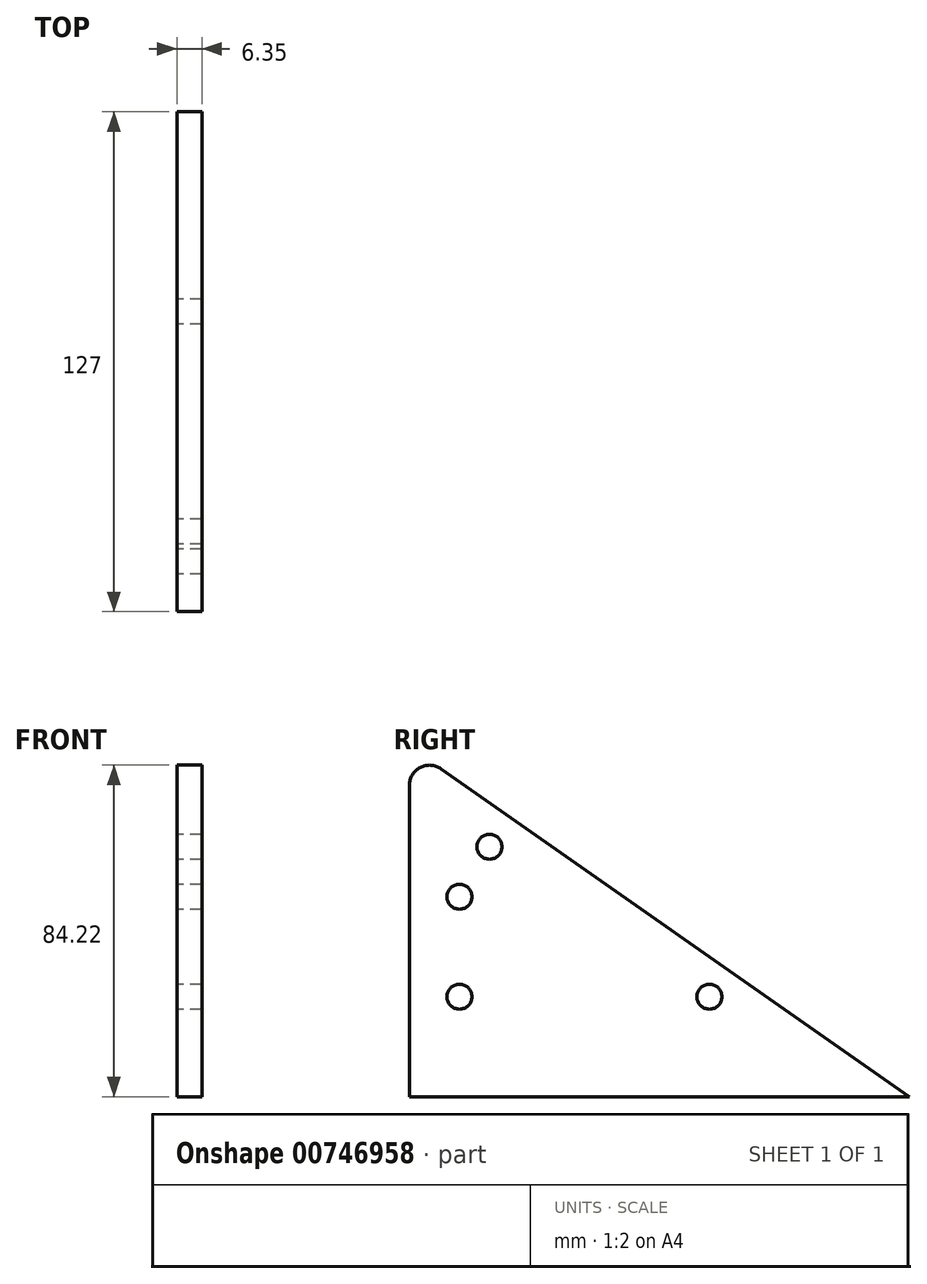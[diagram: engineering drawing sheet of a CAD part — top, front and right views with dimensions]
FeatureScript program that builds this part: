
annotation { "Feature Type Name" : "Feature", "Feature Type Description" : "" }
export const myFeature = defineFeature(function(context is Context, id is Id, definition is map)
    precondition{}
    {
        {
            var Q0;
            Q0=qCreatedBy(makeId("Right.planeOp"),FACE);
            var sketch = newSketch(context, id + "F0", { "sketchPlane" : qUnion([Q0])});
            skLineSegment(sketch, "E0.bottom", {"start": v(63.5, -44.45) * mm, "end": v(-63.5, -44.45) * mm});
            skLineSegment(sketch, "E0.right", {"start": v(-63.5, -44.45) * mm, "end": v(-63.5, 44.45) * mm});
            skPoint(sketch, "E0.middle", {"position": v(0, 0) * mm});
            skLineSegment(sketch, "E1", {"start": v(-63.5, 44.45) * mm, "end": v(63.5, -44.45) * mm});
            skCircle(sketch, "E2", {"center": v(-50.8, -19.05) * mm, "radius": 3.18 * mm});
            skCircle(sketch, "E3", {"center": v(-43.18, 19.05) * mm, "radius": 3.18 * mm});
            skCircle(sketch, "E4", {"center": v(-50.8, 6.35) * mm, "radius": 3.18 * mm});
            skCircle(sketch, "E5", {"center": v(12.7, -19.05) * mm, "radius": 3.18 * mm});
            skPoint(sketch, "E0.left.end.orphan", {"position": v(63.5, 44.45) * mm});
            skSolve(sketch);
        }
        {
            var Q0;
            Q0=makeQuery(id+"F0.imprint","IMPRINT",FACE,{"disambiguationData":[TD([[makeQuery(id+"F0.imprint","IMPRINT",EDGE,{"derivedFrom":sQuery(id+"F0.wireOp",EDGE,"E0.bottom")}),-1.0]])]});
            extrude(context, id + "F1", {"entities" : qUnion([Q0]), "depth" : 6.35 * mm, "offsetDistance" : 25.4 * mm});
        }
        {
            var Q0;
            Q0=makeQuery(id+"F1.opExtrude","SWEPT_EDGE",EDGE,{"disambiguationData":[OSD([sQuery(id+"F0.wireOp",EDGE,"E0.right"),sQuery(id+"F0.wireOp",EDGE,"E1")])]});
            fillet(context, id + "F2", {"entities" : qUnion([Q0]), "radius" : 5.08 * mm, "tangentPropagation" : true, "allowEdgeOverflow" : false});
        }
    });
